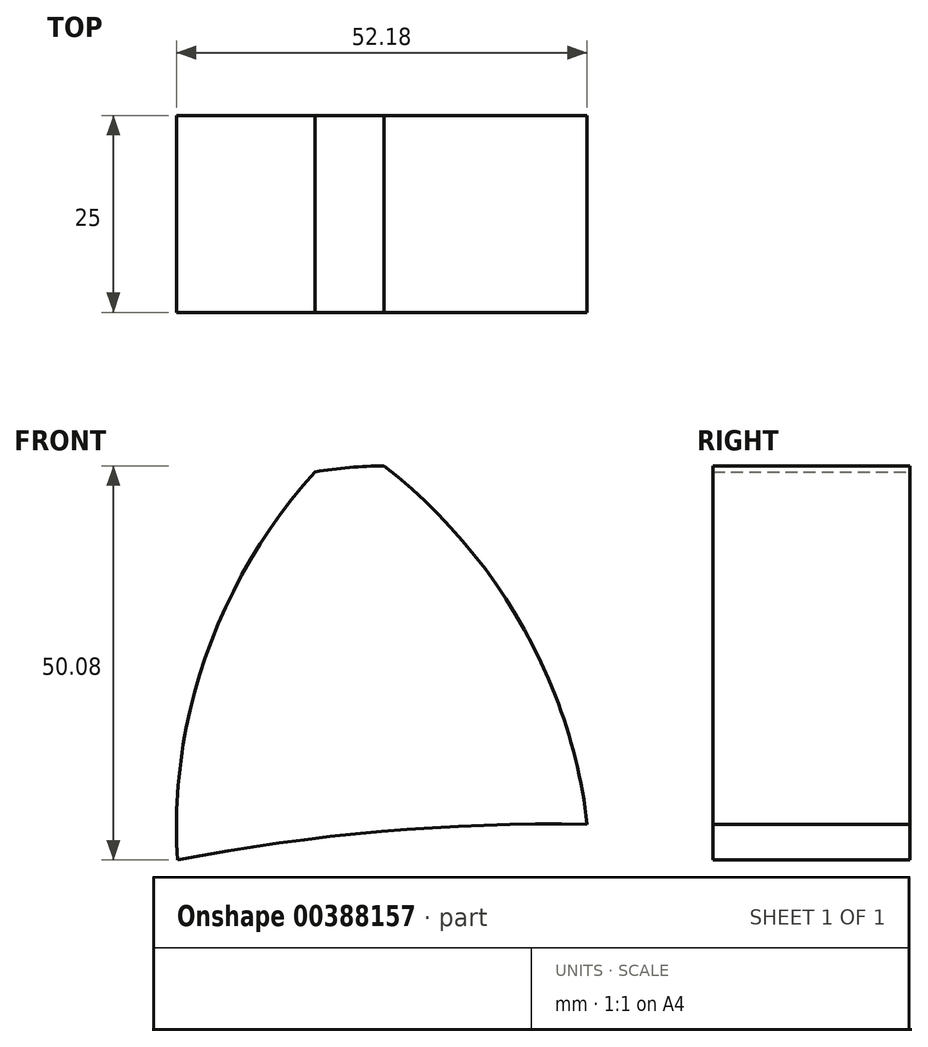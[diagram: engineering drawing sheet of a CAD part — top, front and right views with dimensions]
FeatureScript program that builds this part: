
annotation { "Feature Type Name" : "Feature", "Feature Type Description" : "" }
export const myFeature = defineFeature(function(context is Context, id is Id, definition is map)
    precondition{}
    {
        {
            var Q0;
            Q0=qCreatedBy(makeId("Front.planeOp"),FACE);
            var sketch = newSketch(context, id + "F0", { "sketchPlane" : qUnion([Q0])});
            skCircle(sketch, "E0", {"center": v(0, 0) * mm, "radius": 300 * mm, "construction": true});
            skCircle(sketch, "E1", {"center": v(0, 0) * mm, "radius": 270 * mm, "construction": true});
            skCircle(sketch, "E2", {"center": v(0, 0) * mm, "radius": 253.5 * mm, "construction": true});
            skLineSegment(sketch, "E3", {"start": v(0, 0) * mm, "end": v(0, 414.93) * mm, "construction": true});
            skLineSegment(sketch, "E4", {"start": v(0, 0) * mm, "end": v(-36.4, 416.1) * mm, "construction": true});
            skLineSegment(sketch, "E5", {"start": v(0, 270) * mm, "end": v(-427.1, 270) * mm, "construction": true});
            skLineSegment(sketch, "E6", {"start": v(0, 270) * mm, "end": v(-407.51, 121.68) * mm, "construction": true});
            skCircle(sketch, "E7", {"center": v(0, 270) * mm, "radius": 67.5 * mm, "construction": true});
            skCircle(sketch, "E8", {"center": v(0, 0) * mm, "radius": 253.72 * mm});
            skCircle(sketch, "E9", {"center": v(-63, 245.77) * mm, "radius": 67.5 * mm, "construction": true});
            skArc(sketch, "E10", {"start": v(0, 270) * mm, "mid": v(-8.9, 286.08) * mm, "end": v(-21.76, 299.2) * mm});
            skArc(sketch, "E11", {"start": v(4.06, 253.47) * mm, "mid": v(2.57, 261.87) * mm, "end": v(0, 270) * mm});
            skArc(sketch, "E12.MirrorCS", {"start": v(-46.89, 265.9) * mm, "mid": v(-40.9, 283.28) * mm, "end": v(-30.52, 298.44) * mm});
            skArc(sketch, "E13.MirrorCS", {"start": v(-48.01, 248.91) * mm, "mid": v(-48, 257.44) * mm, "end": v(-46.89, 265.9) * mm});
            skArc(sketch, "E14", {"start": v(-21.76, 299.2) * mm, "mid": v(-26.16, 299) * mm, "end": v(-30.52, 298.44) * mm});
            skCircle(sketch, "E15", {"center": v(0, 0) * mm, "radius": 232.5 * mm, "construction": true});
            skSolve(sketch);
        }
        {
            var Q0;
            {var subQ2=sQuery(id+"F0.wireOp",EDGE,"E10");Q0=makeQuery(id+"F0.imprint","IMPRINT",FACE,{"disambiguationData":[TD([[makeQuery(id+"F0.imprint","IMPRINT",EDGE,{"derivedFrom":subQ2}),1.0]])]});}
            extrude(context, id + "F1", {"entities" : qUnion([Q0]), "depth" : 25 * mm});
        }
    });
